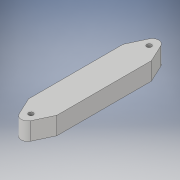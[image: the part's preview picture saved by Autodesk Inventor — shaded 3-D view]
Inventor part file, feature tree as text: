
AUTODESK INVENTOR PART (.ipt)
format: ipt  version: 2019 (Build 230136000, 136)  size: 135,168 bytes
history: native  units: mm
features: sketch x3, extrude x2, hole x1
ambient origin geometry x8: Origin, YZ Plane, XZ Plane, XY Plane, X Axis, Y Axis, Z Axis, Center Point
bodies: Solid1 (feature_tree)
feature tree (6):
  sketch  "Sketch1"  dims[d0=15.0mm d1=35.0mm]
  extrude  "Extrusion1"  Depth=35.0mm
  extrude  "Extrusion2"  Depth=35.0mm
  hole  "Hole1"  [1 undecoded]
  sketch  "Sketch2"  dims[d2=15.0mm d3=35.0mm]
  sketch  "Sketch3"  dims[d4=12.0mm d5=12.0mm d6=40.0mm d7=40.0mm d8=15.0mm d9=7.0mm d10=15.0mm d11=7.0mm d12=15.0mm d13=0.0mm d14=10.0mm d15=0.0mm d16=50.0mm d17=50.0mm d18=4.0mm d19=6.0mm d20=5.0mm d21=2.0mm d22=90.0deg d23=8.0mm d24=20.594885mm d25=0.0625mm d26=0.75mm d27=0.375mm]
note: 1 required parameter value undecoded (feature->parameter linkage not recoverable at this tier; creation-order binding heuristic only, values carry confidence <= 0.55)
